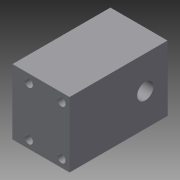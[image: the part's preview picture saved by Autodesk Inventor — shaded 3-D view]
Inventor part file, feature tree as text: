
AUTODESK INVENTOR PART (.ipt)
format: ipt  version: 2014 SP1 (Build 180222100, 222)  size: 99,840 bytes
history: native  units: in
note: dims shown in document units (in); Inventor stores cm internally (conversion verified against a paired STEP export)
features: sketch x3, extrude x2, hole x1
ambient origin geometry x8: Origin, YZ Plane, XZ Plane, XY Plane, X Axis, Y Axis, Z Axis, Center Point
bodies: Solid1 (feature_tree)
feature tree (6):
  extrude  "Extrusion1"  Depth=2.0in
  extrude  "Extrusion2"  Depth=1.75in
  hole  "Hole1"  [1 undecoded]
  sketch  "Sketch1"  dims[d0=3.0in d1=2.0in]
  sketch  "Sketch2"  dims[d2=1.75in d3=0.0in d4=0.5in]
  sketch  "Sketch3"  dims[d5=1.0in d6=2.32in d7=1.5in d8=0.0in d9=0.25in d10=0.25in d11=0.25in d12=0.5in d13=0.5in d14=0.25in d15=0.25in d16=0.25in d17=0.25in d18=0.75in d19=0.375in d20=0.25in d21=0.5635in d22=1.0in d23=0.8108in]
note: 1 required parameter value undecoded (feature->parameter linkage not recoverable at this tier; creation-order binding heuristic only, values carry confidence <= 0.55)
